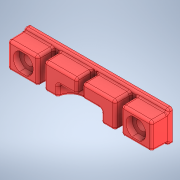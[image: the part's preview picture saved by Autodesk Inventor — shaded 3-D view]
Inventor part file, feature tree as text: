
AUTODESK INVENTOR PART (.ipt)
format: ipt  version: 2022.3 (Build 263350000, 350)  size: 611,840 bytes
history: native  units: in
note: dims shown in document units (in); Inventor stores cm internally (conversion verified against a paired STEP export)
features: fillet x3, extrude x1, sketch x1
ambient origin geometry x8: Origin, YZ Plane, XZ Plane, XY Plane, X Axis, Y Axis, Z Axis, Center Point
bodies: Solid2 (feature_tree), Solid1 (feature_tree)
feature tree (5):
  extrude  "Extrusion1"  TaperAngle=0.0deg  [1 undecoded]
  fillet  "Fillet2"  Radius=0.0625in
  fillet  "Fillet3"  Radius=0.05in
  fillet  "Fillet4"  Radius=0.05in
  sketch  "Sketch1"  dims[d0=0.15in d1=0.0in d2=0.0in d4=0.0625in d5=0.05in d6=0.05in d7=0.0in d8=0.0in]
note: 1 required parameter value undecoded (feature->parameter linkage not recoverable at this tier; creation-order binding heuristic only, values carry confidence <= 0.55)
